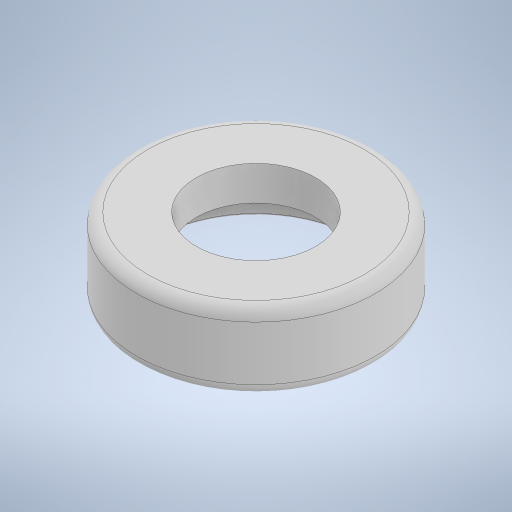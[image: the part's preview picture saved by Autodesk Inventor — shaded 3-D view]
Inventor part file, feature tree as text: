
AUTODESK INVENTOR PART (.ipt)
format: ipt  version: 2024 (Build 280153000, 153)  size: 264,192 bytes
history: native  units: in
note: dims shown in document units (in); Inventor stores cm internally (conversion verified against a paired STEP export)
features: sketch x2, revolve x1, fillet x1, extrude x1
ambient origin geometry x8: Origin, YZ Plane, XZ Plane, XY Plane, X Axis, Y Axis, Z Axis, Center Point
bodies: Solid1 (feature_tree)
feature tree (5):
  revolve  "Revolution1"  [1 undecoded]
  fillet  "Fillet1"  Radius=0.1625in
  extrude  "Extrusion1"  TaperAngle=90.0deg  [1 undecoded]
  sketch  "Sketch1"  dims[d0=0.1625in d1=0.025in d2=0.1625in]
  sketch  "Sketch2"  dims[d3=0.1875in d4=90.0deg d5=0.015in d6=0.1625in d7=0.0in d8=0.0in]
note: 2 required parameter values undecoded (feature->parameter linkage not recoverable at this tier; creation-order binding heuristic only, values carry confidence <= 0.55)